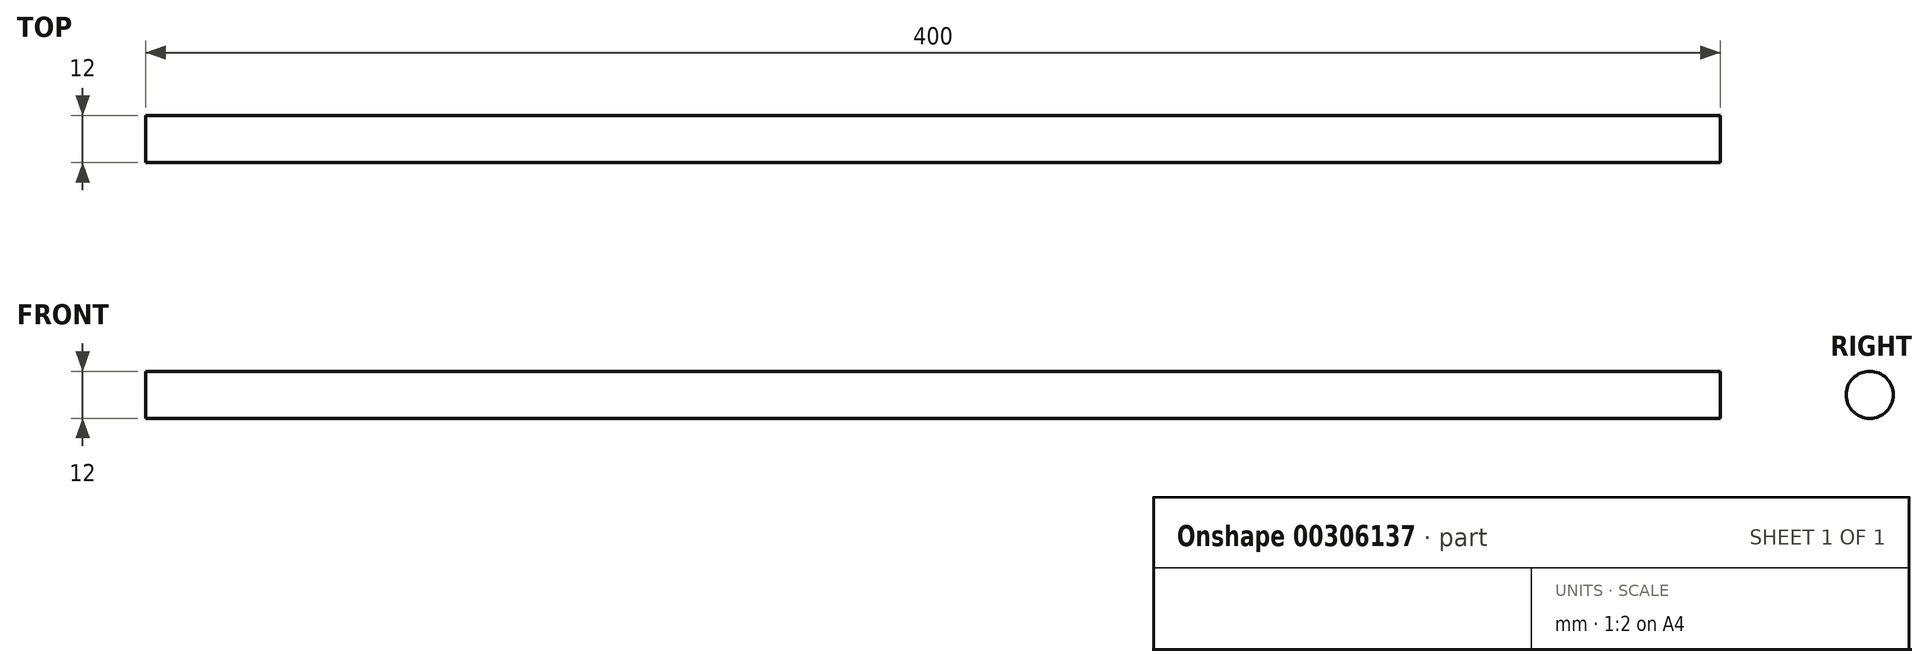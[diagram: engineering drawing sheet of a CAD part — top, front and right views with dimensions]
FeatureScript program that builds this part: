
annotation { "Feature Type Name" : "Feature", "Feature Type Description" : "" }
export const myFeature = defineFeature(function(context is Context, id is Id, definition is map)
    precondition{}
    {
        {
            var Q0;
            Q0=qCreatedBy(makeId("Right.planeOp"),FACE);
            var sketch = newSketch(context, id + "F0", { "sketchPlane" : qUnion([Q0])});
            skCircle(sketch, "E0", {"center": v(0, 0) * mm, "radius": 6 * mm});
            skSolve(sketch);
        }
        {
            var Q0;
            Q0=qSketchRegion(id+"F0",true);
            extrude(context, id + "F1", {"entities" : qUnion([Q0]), "depth" : 400 * mm});
        }
    });
